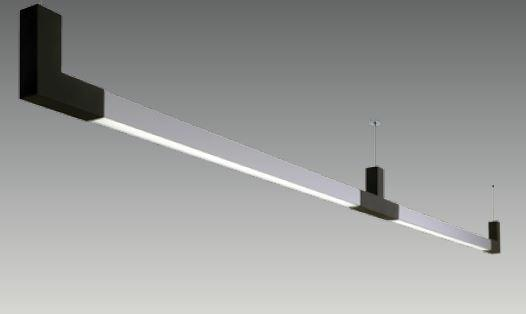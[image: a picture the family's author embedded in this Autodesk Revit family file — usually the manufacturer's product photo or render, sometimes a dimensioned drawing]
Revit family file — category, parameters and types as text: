
# Revit family: SD 3500 PLT
name_source: partatom
category: Lighting Fixtures
revit_build: Autodesk Revit 2017 (Build: 20160225_1515(x64)
units: mm (PartAtom-declared; Revit-internal decimal feet)

## family parameters
Cut with Voids When Loaded = No
Host = Face
Light Source = Yes
Part Type = Normal
Room Calculation Point = No
Round Connector Dimension = Use Diameter
Shared = No

## types (2) — shared parameters
Color Filter = 16777215
Default Elevation = 1219 mm
Dimming Lamp Color Temperature Shift = <None>
Emit Shape Visible in Rendering = Yes
Emit from Rectangle Length = 40 mm  [stored 0.131234 ft]
Emit from Rectangle Width = 1400 mm  [stored 4.59318 ft]
Light Source Symbol Size = 610 mm
Manufacturer = ARLIGHT
Type Image = SD 3500 PLT.JPG
Wattage Comments = 108W

## type names (no varying parameters)
- SDPLT.3500.108.30
- SDPLT.3500.108.40

note: [stored X ft] marks values corroborated as IEEE doubles in the binary element streams (Revit-internal decimal feet)

## geometry (parser evidence)
native form markers: Sweep x3
no freeform markers — native parametric forms only
